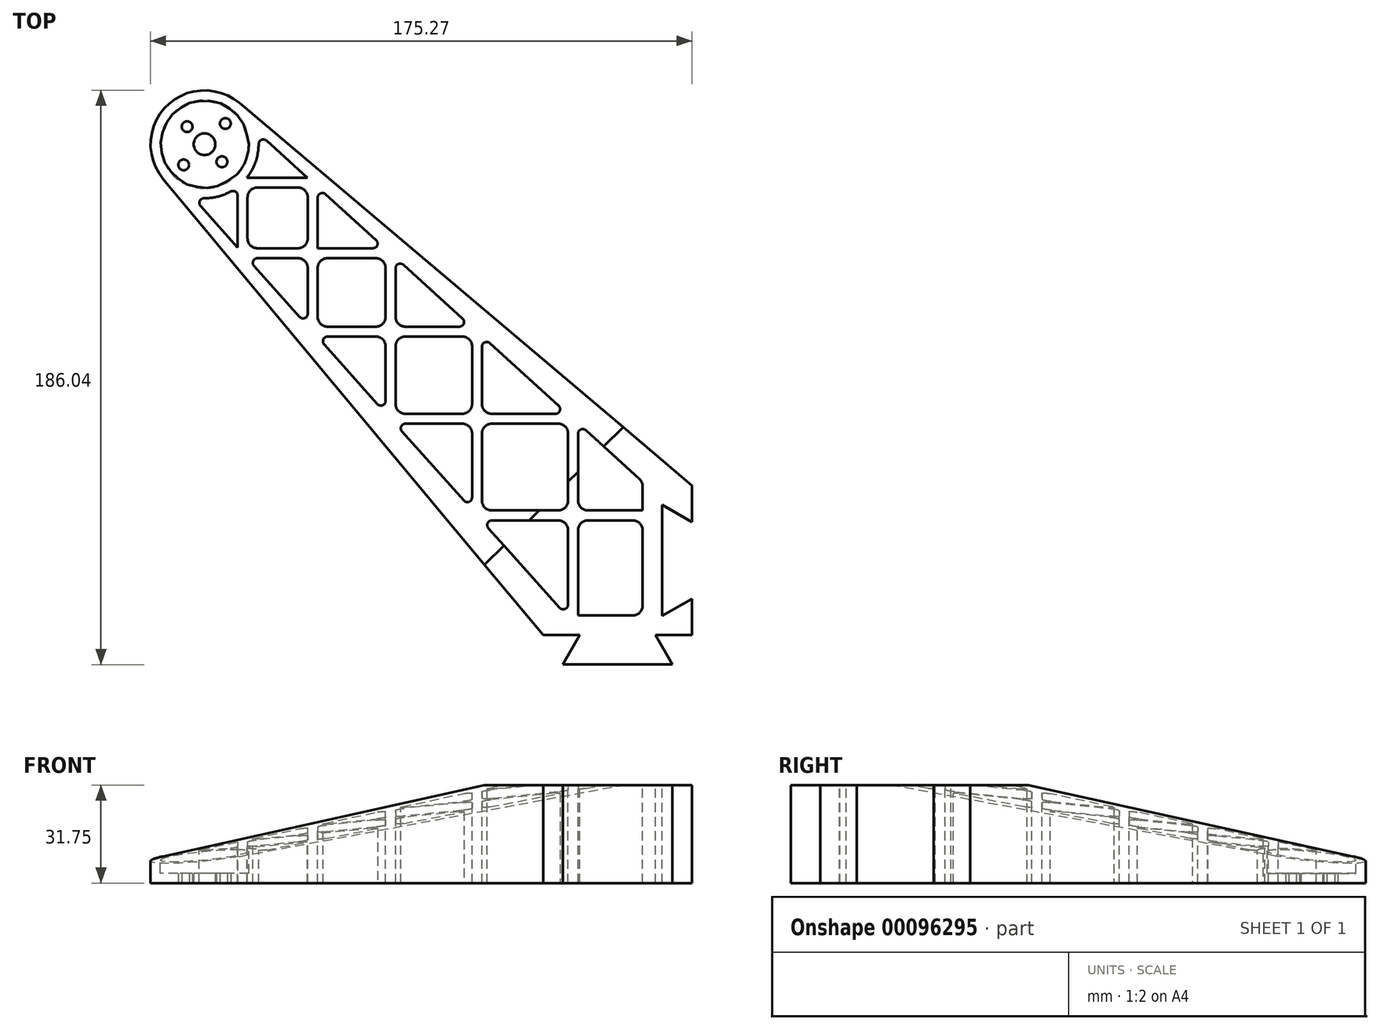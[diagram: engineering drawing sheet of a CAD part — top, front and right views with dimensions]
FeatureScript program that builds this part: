
annotation { "Feature Type Name" : "Feature", "Feature Type Description" : "" }
export const myFeature = defineFeature(function(context is Context, id is Id, definition is map)
    precondition{}
    {
        {
            var Q0;
            Q0=qCreatedBy(makeId("Top.planeOp"),FACE);
            var sketch = newSketch(context, id + "F0", { "sketchPlane" : qUnion([Q0])});
            skCircle(sketch, "E0", {"center": v(-157.77, 159.01) * mm, "radius": 17.5 * mm});
            skLineSegment(sketch, "E1", {"start": v(-157.77, 159.01) * mm, "end": v(0, 0) * mm, "construction": true});
            skLineSegment(sketch, "E2", {"start": v(-171.22, 147.82) * mm, "end": v(-48.17, 0) * mm});
            skLineSegment(sketch, "E3", {"start": v(-146.46, 172.38) * mm, "end": v(0, 48.5) * mm});
            skLineSegment(sketch, "E4", {"start": v(0, 48.5) * mm, "end": v(0, 0) * mm});
            skLineSegment(sketch, "E5", {"start": v(0, 0) * mm, "end": v(-48.17, 0) * mm});
            skSolve(sketch);
        }
        {
            var Q0;
            Q0 = qSketchRegion(id + "F0", true);
            var Q1;
            Q1 = qSketchRegion(id + "F2", true);
            extrude(context, id + "F1", {"entities" : qUnion([Q0, Q1]), "depth" : 31.75 * mm});
        }
        {
            var Q0;
            Q0=makeQuery(id+"F1.opExtrude","CAP_FACE",FACE,{"disambiguationData":[OSD([sQuery(id+"F0.wireOp",EDGE,"E0"),sQuery(id+"F0.wireOp",EDGE,"E2"),sQuery(id+"F0.wireOp",EDGE,"E3"),sQuery(id+"F0.wireOp",EDGE,"E4"),sQuery(id+"F0.wireOp",EDGE,"E5")])],"isStart":false});
            var sketch = newSketch(context, id + "F2", { "sketchPlane" : qUnion([Q0])});
            skCircle(sketch, "E6", {"center": v(-157.77, 159.01) * mm, "radius": 14.33 * mm});
            skSolve(sketch);
        }
        {
            var Q0;
            Q0 = qSketchRegion(id + "F2", true);
            extrude(context, id + "F3", {"entities" : qUnion([Q0]), "operationType" : NewBodyOperationType.REMOVE, "oppositeDirection" : true, "depth" : 28.57 * mm});
        }
        {
            var Q0;
            Q0=makeQuery(id+"F1.opExtrude","CAP_FACE",FACE,{"disambiguationData":[OSD([sQuery(id+"F0.wireOp",EDGE,"E0"),sQuery(id+"F0.wireOp",EDGE,"E2"),sQuery(id+"F0.wireOp",EDGE,"E3"),sQuery(id+"F0.wireOp",EDGE,"E4"),sQuery(id+"F0.wireOp",EDGE,"E5")])],"isStart":false});
            var sketch = newSketch(context, id + "F4", { "sketchPlane" : qUnion([Q0])});
            skLineSegment(sketch, "E7", {"start": v(-36.32, 0) * mm, "end": v(-41.82, -9.52) * mm});
            skLineSegment(sketch, "E8", {"start": v(-41.82, -9.53) * mm, "end": v(-6.35, -9.53) * mm});
            skLineSegment(sketch, "E9", {"start": v(-6.35, -9.53) * mm, "end": v(-11.85, 0) * mm});
            skSolve(sketch);
        }
        {
            var Q0;
            Q0 = qSketchRegion(id + "F4", true);
            var Q1;
            {var subQ0=sQuery(id+"F4.wireOp",EDGE,"E7");Q1=makeQuery(id+"F4.imprint","IMPRINT",FACE,{"disambiguationData":[TD([[makeQuery(id+"F4.imprint","IMPRINT",EDGE,{"derivedFrom":subQ0}),1.0]])]});}
            extrude(context, id + "F5", {"entities" : qUnion([Q0, Q1]), "operationType" : NewBodyOperationType.ADD, "oppositeDirection" : true, "depth" : 31.75 * mm});
        }
        {
            var Q0;
            {var subQ0=sQuery(id+"F0.wireOp",EDGE,"E5");Q0=makeQuery(id+"F5.boolean.opBoolean","MERGE",FACE,{"derivedFrom":[makeQuery(id+"F1.opExtrude","CAP_FACE",FACE,{"disambiguationData":[OSD([sQuery(id+"F0.wireOp",EDGE,"E0"),sQuery(id+"F0.wireOp",EDGE,"E2"),sQuery(id+"F0.wireOp",EDGE,"E3"),sQuery(id+"F0.wireOp",EDGE,"E4"),subQ0])],"isStart":false}),makeQuery(id+"F5.opExtrude","CAP_FACE",FACE,{"disambiguationData":[OSD([subQ0,sQuery(id+"F4.wireOp",EDGE,"E7"),sQuery(id+"F4.wireOp",EDGE,"E8"),sQuery(id+"F4.wireOp",EDGE,"E9")])],"isStart":true})]});}
            var sketch = newSketch(context, id + "F6", { "sketchPlane" : qUnion([Q0])});
            skLineSegment(sketch, "E10", {"start": v(0, 11.8) * mm, "end": v(-9.65, 6.22) * mm});
            skLineSegment(sketch, "E11", {"start": v(-9.65, 6.22) * mm, "end": v(-9.65, 42.27) * mm});
            skLineSegment(sketch, "E12", {"start": v(-9.65, 42.27) * mm, "end": v(0, 36.7) * mm});
            skSolve(sketch);
        }
        {
            var Q0;
            Q0 = qSketchRegion(id + "F6", true);
            var Q1;
            {var subQ0=sQuery(id+"F6.wireOp",EDGE,"E10");Q1=makeQuery(id+"F6.imprint","IMPRINT",FACE,{"disambiguationData":[TD([[makeQuery(id+"F6.imprint","IMPRINT",EDGE,{"derivedFrom":subQ0}),-1.0]])]});}
            extrude(context, id + "F7", {"entities" : qUnion([Q0, Q1]), "operationType" : NewBodyOperationType.REMOVE, "endBound" : BoundingType.THROUGH_ALL, "oppositeDirection" : true, "depth" : 25.4 * mm});
        }
        {
            var Q0;
            {var subQ0=sQuery(id+"F0.wireOp",EDGE,"E5");Q0=makeQuery(id+"F5.boolean.opBoolean","MERGE",FACE,{"derivedFrom":[makeQuery(id+"F1.opExtrude","CAP_FACE",FACE,{"disambiguationData":[OSD([sQuery(id+"F0.wireOp",EDGE,"E0"),sQuery(id+"F0.wireOp",EDGE,"E2"),sQuery(id+"F0.wireOp",EDGE,"E3"),sQuery(id+"F0.wireOp",EDGE,"E4"),subQ0])],"isStart":false}),makeQuery(id+"F5.opExtrude","CAP_FACE",FACE,{"disambiguationData":[OSD([subQ0,sQuery(id+"F4.wireOp",EDGE,"E7"),sQuery(id+"F4.wireOp",EDGE,"E8"),sQuery(id+"F4.wireOp",EDGE,"E9")])],"isStart":true})]});}
            var sketch = newSketch(context, id + "F8", { "sketchPlane" : qUnion([Q0])});
            skCircle(sketch, "E13", {"center": v(-157.77, 159.01) * mm, "radius": 17.5 * mm});
            skLineSegment(sketch, "E14", {"start": v(-40.6, 6.35) * mm, "end": v(-168.45, 149.47) * mm});
            skLineSegment(sketch, "E15", {"start": v(-40.6, 6.35) * mm, "end": v(-16, 6.35) * mm});
            skLineSegment(sketch, "E16", {"start": v(-16, 6.35) * mm, "end": v(-16, 49.7) * mm});
            skLineSegment(sketch, "E17", {"start": v(-16, 49.7) * mm, "end": v(-148.14, 169.62) * mm});
            skSolve(sketch);
        }
        {
            var Q0;
            {var subQ1=sQuery(id+"F8.wireOp",EDGE,"E15");Q0=makeQuery(id+"F8.imprint","IMPRINT",FACE,{"disambiguationData":[TD([[makeQuery(id+"F8.imprint","IMPRINT",EDGE,{"derivedFrom":subQ1}),1.0]])]});}
            extrude(context, id + "F9", {"entities" : qUnion([Q0]), "operationType" : NewBodyOperationType.REMOVE, "endBound" : BoundingType.THROUGH_ALL, "oppositeDirection" : true, "depth" : 28.57 * mm});
        }
        {
            var Q0;
            {var subQ0=sQuery(id+"F0.wireOp",EDGE,"E5");Q0=makeQuery(id+"F5.boolean.opBoolean","MERGE",FACE,{"derivedFrom":[makeQuery(id+"F1.opExtrude","CAP_FACE",FACE,{"disambiguationData":[OSD([sQuery(id+"F0.wireOp",EDGE,"E0"),sQuery(id+"F0.wireOp",EDGE,"E2"),sQuery(id+"F0.wireOp",EDGE,"E3"),sQuery(id+"F0.wireOp",EDGE,"E4"),subQ0])],"isStart":false}),makeQuery(id+"F5.opExtrude","CAP_FACE",FACE,{"disambiguationData":[OSD([subQ0,sQuery(id+"F4.wireOp",EDGE,"E7"),sQuery(id+"F4.wireOp",EDGE,"E8"),sQuery(id+"F4.wireOp",EDGE,"E9")])],"isStart":true})]});}
            var sketch = newSketch(context, id + "F10", { "sketchPlane" : qUnion([Q0])});
            skLineSegment(sketch, "E18", {"start": v(-145.44, 146.6) * mm, "end": v(-122.76, 146.6) * mm, "construction": true});
            skLineSegment(sketch, "E19", {"start": v(-122.76, 146.6) * mm, "end": v(-122.76, 98.33) * mm, "construction": true});
            skLineSegment(sketch, "E20", {"start": v(-122.76, 98.33) * mm, "end": v(-69.58, 98.33) * mm, "construction": true});
            skLineSegment(sketch, "E21", {"start": v(-69.58, 98.33) * mm, "end": v(-69.58, 38.8) * mm, "construction": true});
            skLineSegment(sketch, "E22", {"start": v(-69.58, 38.8) * mm, "end": v(-16, 38.8) * mm, "construction": true});
            skLineSegment(sketch, "E23", {"start": v(-145.44, 146.6) * mm, "end": v(-145.44, 123.71) * mm, "construction": true});
            skLineSegment(sketch, "E24", {"start": v(-145.44, 123.71) * mm, "end": v(-97.56, 123.71) * mm, "construction": true});
            skLineSegment(sketch, "E25", {"start": v(-97.56, 123.71) * mm, "end": v(-97.56, 70.1) * mm, "construction": true});
            skLineSegment(sketch, "E26", {"start": v(-97.56, 70.1) * mm, "end": v(-38.5, 70.1) * mm, "construction": true});
            skLineSegment(sketch, "E27", {"start": v(-38.5, 70.1) * mm, "end": v(-38.5, 6.35) * mm, "construction": true});
            skArc(sketch, "E28.0", {"start": v(-161.75, 141.98) * mm, "mid": v(-145.44, 146.6) * mm, "end": v(-140.7, 162.87) * mm});
            skLineSegment(sketch, "E29.0", {"start": v(-16, 49.7) * mm, "end": v(-140.7, 162.87) * mm});
            skLineSegment(sketch, "E30.0", {"start": v(-40.6, 6.35) * mm, "end": v(-161.75, 141.98) * mm});
            skLineSegment(sketch, "E31.0", {"start": v(-144.01, 148.2) * mm, "end": v(-124.53, 148.2) * mm});
            skLineSegment(sketch, "E32", {"start": v(-147.04, 145.19) * mm, "end": v(-147.04, 125.5) * mm});
            skLineSegment(sketch, "E33.bottom", {"start": v(-121.16, 122.11) * mm, "end": v(-99.16, 122.11) * mm});
            skLineSegment(sketch, "E33.top", {"start": v(-121.16, 99.93) * mm, "end": v(-99.16, 99.93) * mm});
            skLineSegment(sketch, "E33.left", {"start": v(-121.16, 122.11) * mm, "end": v(-121.16, 99.93) * mm});
            skLineSegment(sketch, "E33.right", {"start": v(-99.16, 122.11) * mm, "end": v(-99.16, 99.93) * mm});
            skLineSegment(sketch, "E34.bottom", {"start": v(-143.84, 145) * mm, "end": v(-124.36, 145) * mm});
            skLineSegment(sketch, "E34.top", {"start": v(-143.84, 125.31) * mm, "end": v(-124.36, 125.31) * mm});
            skLineSegment(sketch, "E34.left", {"start": v(-143.84, 145) * mm, "end": v(-143.84, 125.31) * mm});
            skLineSegment(sketch, "E34.right", {"start": v(-124.36, 145) * mm, "end": v(-124.36, 125.31) * mm});
            skLineSegment(sketch, "E35.bottom", {"start": v(-95.96, 96.73) * mm, "end": v(-71.18, 96.73) * mm});
            skLineSegment(sketch, "E35.top", {"start": v(-95.96, 71.7) * mm, "end": v(-71.18, 71.7) * mm});
            skLineSegment(sketch, "E35.left", {"start": v(-95.96, 96.73) * mm, "end": v(-95.96, 71.7) * mm});
            skLineSegment(sketch, "E35.right", {"start": v(-71.18, 96.73) * mm, "end": v(-71.18, 71.7) * mm});
            skLineSegment(sketch, "E36.bottom", {"start": v(-67.98, 68.5) * mm, "end": v(-40.1, 68.5) * mm});
            skLineSegment(sketch, "E36.top", {"start": v(-67.98, 40.4) * mm, "end": v(-40.1, 40.4) * mm});
            skLineSegment(sketch, "E36.left", {"start": v(-67.98, 68.5) * mm, "end": v(-67.98, 40.4) * mm});
            skLineSegment(sketch, "E36.right", {"start": v(-40.1, 68.5) * mm, "end": v(-40.1, 40.4) * mm});
            skLineSegment(sketch, "E37.bottom", {"start": v(-36.89, 37.2) * mm, "end": v(-16, 37.2) * mm});
            skLineSegment(sketch, "E37.left", {"start": v(-36.89, 37.2) * mm, "end": v(-36.89, 6.35) * mm});
            skLineSegment(sketch, "E38.top", {"start": v(-36.89, 40.4) * mm, "end": v(-16, 40.4) * mm});
            skLineSegment(sketch, "E38.left", {"start": v(-36.89, 68.66) * mm, "end": v(-36.89, 40.4) * mm});
            skLineSegment(sketch, "E39.top", {"start": v(-40.1, 37.2) * mm, "end": v(-68.15, 37.2) * mm});
            skLineSegment(sketch, "E39.left", {"start": v(-40.1, 6.35) * mm, "end": v(-40.1, 37.2) * mm});
            skLineSegment(sketch, "E40.top", {"start": v(-71.18, 68.5) * mm, "end": v(-96.13, 68.5) * mm});
            skLineSegment(sketch, "E40.left", {"start": v(-71.18, 40.59) * mm, "end": v(-71.18, 68.5) * mm});
            skLineSegment(sketch, "E41.top", {"start": v(-67.98, 71.7) * mm, "end": v(-40.25, 71.7) * mm});
            skLineSegment(sketch, "E41.left", {"start": v(-67.98, 96.88) * mm, "end": v(-67.98, 71.7) * mm});
            skLineSegment(sketch, "E42.top", {"start": v(-99.16, 96.73) * mm, "end": v(-121.33, 96.73) * mm});
            skLineSegment(sketch, "E42.left", {"start": v(-99.16, 71.9) * mm, "end": v(-99.16, 96.73) * mm});
            skLineSegment(sketch, "E43.top", {"start": v(-95.96, 99.93) * mm, "end": v(-71.35, 99.93) * mm});
            skLineSegment(sketch, "E43.left", {"start": v(-95.96, 122.26) * mm, "end": v(-95.96, 99.93) * mm});
            skLineSegment(sketch, "E44.top", {"start": v(-121.16, 125.31) * mm, "end": v(-99.32, 125.31) * mm});
            skLineSegment(sketch, "E44.left", {"start": v(-121.16, 145.14) * mm, "end": v(-121.16, 125.31) * mm});
            skLineSegment(sketch, "E45.top", {"start": v(-124.36, 122.11) * mm, "end": v(-144.01, 122.11) * mm});
            skLineSegment(sketch, "E45.left", {"start": v(-124.36, 100.12) * mm, "end": v(-124.36, 122.11) * mm});
            skLineSegment(sketch, "E46.0", {"start": v(-16, 6.35) * mm, "end": v(-16, 49.7) * mm});
            skLineSegment(sketch, "E47.0", {"start": v(-40.6, 6.35) * mm, "end": v(-16, 6.35) * mm});
            skSolve(sketch);
        }
        {
            var Q0;
            {var subQ1=sQuery(id+"F10.wireOp",EDGE,"E31.0");Q0=makeQuery(id+"F10.imprint","IMPRINT",FACE,{"disambiguationData":[TD([[makeQuery(id+"F10.imprint","IMPRINT",EDGE,{"derivedFrom":subQ1}),-1.0]])]});}
            var Q1;
            {var subQ0=sQuery(id+"F0.wireOp",EDGE,"E5");Q1=makeQuery(id+"F5.boolean.opBoolean","MERGE",FACE,{"derivedFrom":[makeQuery(id+"F1.opExtrude","CAP_FACE",FACE,{"disambiguationData":[OSD([sQuery(id+"F0.wireOp",EDGE,"E0"),sQuery(id+"F0.wireOp",EDGE,"E2"),sQuery(id+"F0.wireOp",EDGE,"E3"),sQuery(id+"F0.wireOp",EDGE,"E4"),subQ0])],"isStart":true}),makeQuery(id+"F5.opExtrude","CAP_FACE",FACE,{"disambiguationData":[OSD([subQ0,sQuery(id+"F4.wireOp",EDGE,"E7"),sQuery(id+"F4.wireOp",EDGE,"E8"),sQuery(id+"F4.wireOp",EDGE,"E9")])],"isStart":false})]});}
            extrude(context, id + "F11", {"entities" : qUnion([Q0]), "operationType" : NewBodyOperationType.ADD, "endBound" : BoundingType.UP_TO_SURFACE, "oppositeDirection" : true, "endBoundEntityFace" : qUnion([Q1]), "depth" : 25.4 * mm});
        }
        {
            var Q0;
            Q0=makeQuery(id+"F11.opExtrude","SWEPT_EDGE",EDGE,{"disambiguationData":[OSD([sQuery(id+"F10.wireOp",EDGE,"E28.0"),sQuery(id+"F10.wireOp",EDGE,"E32")])]});
            var Q1;
            Q1=makeQuery(id+"F9.boolean.opBoolean","COPY",EDGE,{"derivedFrom":makeQuery(id+"F9.opExtrude","SWEPT_EDGE",EDGE,{"disambiguationData":[OSD([sQuery(id+"F8.wireOp",EDGE,"E13"),sQuery(id+"F8.wireOp",EDGE,"E14")])]})});
            var Q2;
            Q2=makeQuery(id+"F11.opExtrude","SWEPT_EDGE",EDGE,{"disambiguationData":[OSD([sQuery(id+"F10.wireOp",EDGE,"E30.0"),sQuery(id+"F10.wireOp",EDGE,"E32")])]});
            var Q3;
            Q3=makeQuery(id+"F9.boolean.opBoolean","COPY",EDGE,{"derivedFrom":makeQuery(id+"F9.opExtrude","SWEPT_EDGE",EDGE,{"disambiguationData":[OSD([sQuery(id+"F8.wireOp",EDGE,"E13"),sQuery(id+"F8.wireOp",EDGE,"E17")])]})});
            var Q4;
            Q4=makeQuery(id+"F11.opExtrude","SWEPT_EDGE",EDGE,{"disambiguationData":[OSD([sQuery(id+"F10.wireOp",EDGE,"E28.0"),sQuery(id+"F10.wireOp",EDGE,"E31.0")])]});
            var Q5;
            Q5=makeQuery(id+"F11.opExtrude","SWEPT_EDGE",EDGE,{"disambiguationData":[OSD([sQuery(id+"F10.wireOp",EDGE,"E29.0"),sQuery(id+"F10.wireOp",EDGE,"E31.0")])]});
            fillet(context, id + "F12", {"entities" : qUnion([Q0, Q1, Q2, Q3, Q4, Q5]), "radius" : 1.52 * mm, "tangentPropagation" : true, "allowEdgeOverflow" : false});
        }
        {
            var Q0;
            Q0=makeQuery(id+"F11.opExtrude","SWEPT_EDGE",EDGE,{"disambiguationData":[OSD([sQuery(id+"F10.wireOp",EDGE,"E30.0"),sQuery(id+"F10.wireOp",EDGE,"E45.left")])]});
            var Q1;
            Q1=makeQuery(id+"F11.opExtrude","SWEPT_EDGE",EDGE,{"disambiguationData":[OSD([sQuery(id+"F10.wireOp",EDGE,"E30.0"),sQuery(id+"F10.wireOp",EDGE,"E45.top")])]});
            var Q2;
            Q2=makeQuery(id+"F11.opExtrude","SWEPT_EDGE",EDGE,{"disambiguationData":[OSD([sQuery(id+"F10.wireOp",EDGE,"E30.0"),sQuery(id+"F10.wireOp",EDGE,"E42.top")])]});
            var Q3;
            Q3=makeQuery(id+"F11.opExtrude","SWEPT_EDGE",EDGE,{"disambiguationData":[OSD([sQuery(id+"F10.wireOp",EDGE,"E30.0"),sQuery(id+"F10.wireOp",EDGE,"E42.left")])]});
            var Q4;
            Q4=makeQuery(id+"F11.opExtrude","SWEPT_EDGE",EDGE,{"disambiguationData":[OSD([sQuery(id+"F10.wireOp",EDGE,"E30.0"),sQuery(id+"F10.wireOp",EDGE,"E40.left")])]});
            var Q5;
            Q5=makeQuery(id+"F11.opExtrude","SWEPT_EDGE",EDGE,{"disambiguationData":[OSD([sQuery(id+"F10.wireOp",EDGE,"E30.0"),sQuery(id+"F10.wireOp",EDGE,"E40.top")])]});
            var Q6;
            Q6=makeQuery(id+"F11.opExtrude","SWEPT_EDGE",EDGE,{"disambiguationData":[OSD([sQuery(id+"F10.wireOp",EDGE,"E29.0"),sQuery(id+"F10.wireOp",EDGE,"E43.left")])]});
            var Q7;
            Q7=makeQuery(id+"F11.opExtrude","SWEPT_EDGE",EDGE,{"disambiguationData":[OSD([sQuery(id+"F10.wireOp",EDGE,"E29.0"),sQuery(id+"F10.wireOp",EDGE,"E44.left")])]});
            var Q8;
            Q8=makeQuery(id+"F11.opExtrude","SWEPT_EDGE",EDGE,{"disambiguationData":[OSD([sQuery(id+"F10.wireOp",EDGE,"E29.0"),sQuery(id+"F10.wireOp",EDGE,"E41.left")])]});
            var Q9;
            Q9=makeQuery(id+"F11.opExtrude","SWEPT_EDGE",EDGE,{"disambiguationData":[OSD([sQuery(id+"F10.wireOp",EDGE,"E29.0"),sQuery(id+"F10.wireOp",EDGE,"E44.top")])]});
            var Q10;
            Q10=makeQuery(id+"F11.opExtrude","SWEPT_EDGE",EDGE,{"disambiguationData":[OSD([sQuery(id+"F10.wireOp",EDGE,"E29.0"),sQuery(id+"F10.wireOp",EDGE,"E43.top")])]});
            var Q11;
            Q11=makeQuery(id+"F11.opExtrude","SWEPT_EDGE",EDGE,{"disambiguationData":[OSD([sQuery(id+"F10.wireOp",EDGE,"E29.0"),sQuery(id+"F10.wireOp",EDGE,"E41.top")])]});
            var Q12;
            Q12=makeQuery(id+"F11.opExtrude","SWEPT_EDGE",EDGE,{"disambiguationData":[OSD([sQuery(id+"F10.wireOp",EDGE,"E30.0"),sQuery(id+"F10.wireOp",EDGE,"E39.top")])]});
            var Q13;
            Q13=makeQuery(id+"F11.opExtrude","SWEPT_EDGE",EDGE,{"disambiguationData":[OSD([sQuery(id+"F10.wireOp",EDGE,"E29.0"),sQuery(id+"F10.wireOp",EDGE,"E38.left")])]});
            fillet(context, id + "F13", {"entities" : qUnion([Q0, Q1, Q2, Q3, Q4, Q5, Q6, Q7, Q8, Q9, Q10, Q11, Q12, Q13]), "radius" : 1.52 * mm, "tangentPropagation" : true, "allowEdgeOverflow" : false});
        }
        {
            var Q0;
            Q0=makeQuery(id+"F11.opExtrude","SWEPT_EDGE",EDGE,{"disambiguationData":[OSD([sQuery(id+"F10.wireOp",EDGE,"E36.top"),sQuery(id+"F10.wireOp",EDGE,"E36.right")])]});
            var Q1;
            Q1=makeQuery(id+"F11.opExtrude","SWEPT_EDGE",EDGE,{"disambiguationData":[OSD([sQuery(id+"F10.wireOp",EDGE,"E36.top"),sQuery(id+"F10.wireOp",EDGE,"E36.left")])]});
            var Q2;
            Q2=makeQuery(id+"F11.opExtrude","SWEPT_EDGE",EDGE,{"disambiguationData":[OSD([sQuery(id+"F10.wireOp",EDGE,"E36.bottom"),sQuery(id+"F10.wireOp",EDGE,"E36.left")])]});
            var Q3;
            Q3=makeQuery(id+"F11.opExtrude","SWEPT_EDGE",EDGE,{"disambiguationData":[OSD([sQuery(id+"F10.wireOp",EDGE,"E36.bottom"),sQuery(id+"F10.wireOp",EDGE,"E36.right")])]});
            var Q4;
            Q4=makeQuery(id+"F11.opExtrude","SWEPT_EDGE",EDGE,{"disambiguationData":[OSD([sQuery(id+"F10.wireOp",EDGE,"E39.top"),sQuery(id+"F10.wireOp",EDGE,"E39.left")])]});
            var Q5;
            Q5=makeQuery(id+"F11.opExtrude","SWEPT_EDGE",EDGE,{"disambiguationData":[OSD([sQuery(id+"F10.wireOp",EDGE,"E37.bottom"),sQuery(id+"F10.wireOp",EDGE,"E46.0")])]});
            var Q6;
            Q6=makeQuery(id+"F11.opExtrude","SWEPT_EDGE",EDGE,{"disambiguationData":[OSD([sQuery(id+"F10.wireOp",EDGE,"E37.bottom"),sQuery(id+"F10.wireOp",EDGE,"E37.left")])]});
            var Q7;
            Q7=makeQuery(id+"F11.opExtrude","SWEPT_EDGE",EDGE,{"disambiguationData":[OSD([sQuery(id+"F10.wireOp",EDGE,"E37.left"),sQuery(id+"F10.wireOp",EDGE,"E47.0")])]});
            var Q8;
            Q8=makeQuery(id+"F9.boolean.opBoolean","COPY",EDGE,{"derivedFrom":makeQuery(id+"F9.opExtrude","SWEPT_EDGE",EDGE,{"disambiguationData":[OSD([sQuery(id+"F8.wireOp",EDGE,"E15"),sQuery(id+"F8.wireOp",EDGE,"E16")])]})});
            var Q9;
            Q9=makeQuery(id+"F11.opExtrude","SWEPT_EDGE",EDGE,{"disambiguationData":[OSD([sQuery(id+"F10.wireOp",EDGE,"E40.top"),sQuery(id+"F10.wireOp",EDGE,"E40.left")])]});
            var Q10;
            Q10=makeQuery(id+"F11.opExtrude","SWEPT_EDGE",EDGE,{"disambiguationData":[OSD([sQuery(id+"F10.wireOp",EDGE,"E35.top"),sQuery(id+"F10.wireOp",EDGE,"E35.right")])]});
            var Q11;
            Q11=makeQuery(id+"F11.opExtrude","SWEPT_EDGE",EDGE,{"disambiguationData":[OSD([sQuery(id+"F10.wireOp",EDGE,"E41.top"),sQuery(id+"F10.wireOp",EDGE,"E41.left")])]});
            var Q12;
            Q12=makeQuery(id+"F11.opExtrude","SWEPT_EDGE",EDGE,{"disambiguationData":[OSD([sQuery(id+"F10.wireOp",EDGE,"E35.top"),sQuery(id+"F10.wireOp",EDGE,"E35.left")])]});
            var Q13;
            Q13=makeQuery(id+"F11.opExtrude","SWEPT_EDGE",EDGE,{"disambiguationData":[OSD([sQuery(id+"F10.wireOp",EDGE,"E35.bottom"),sQuery(id+"F10.wireOp",EDGE,"E35.left")])]});
            var Q14;
            Q14=makeQuery(id+"F11.opExtrude","SWEPT_EDGE",EDGE,{"disambiguationData":[OSD([sQuery(id+"F10.wireOp",EDGE,"E35.bottom"),sQuery(id+"F10.wireOp",EDGE,"E35.right")])]});
            var Q15;
            Q15=makeQuery(id+"F11.opExtrude","SWEPT_EDGE",EDGE,{"disambiguationData":[OSD([sQuery(id+"F10.wireOp",EDGE,"E42.top"),sQuery(id+"F10.wireOp",EDGE,"E42.left")])]});
            var Q16;
            Q16=makeQuery(id+"F11.opExtrude","SWEPT_EDGE",EDGE,{"disambiguationData":[OSD([sQuery(id+"F10.wireOp",EDGE,"E33.bottom"),sQuery(id+"F10.wireOp",EDGE,"E33.right")])]});
            var Q17;
            Q17=makeQuery(id+"F11.opExtrude","SWEPT_EDGE",EDGE,{"disambiguationData":[OSD([sQuery(id+"F10.wireOp",EDGE,"E45.top"),sQuery(id+"F10.wireOp",EDGE,"E45.left")])]});
            var Q18;
            Q18=makeQuery(id+"F11.opExtrude","SWEPT_EDGE",EDGE,{"disambiguationData":[OSD([sQuery(id+"F10.wireOp",EDGE,"E34.bottom"),sQuery(id+"F10.wireOp",EDGE,"E34.right")])]});
            var Q19;
            Q19=makeQuery(id+"F11.opExtrude","SWEPT_EDGE",EDGE,{"disambiguationData":[OSD([sQuery(id+"F10.wireOp",EDGE,"E43.top"),sQuery(id+"F10.wireOp",EDGE,"E43.left")])]});
            var Q20;
            Q20=makeQuery(id+"F11.opExtrude","SWEPT_EDGE",EDGE,{"disambiguationData":[OSD([sQuery(id+"F10.wireOp",EDGE,"E33.top"),sQuery(id+"F10.wireOp",EDGE,"E33.left")])]});
            var Q21;
            Q21=makeQuery(id+"F11.opExtrude","SWEPT_EDGE",EDGE,{"disambiguationData":[OSD([sQuery(id+"F10.wireOp",EDGE,"E34.top"),sQuery(id+"F10.wireOp",EDGE,"E34.left")])]});
            var Q22;
            Q22=makeQuery(id+"F11.opExtrude","SWEPT_EDGE",EDGE,{"disambiguationData":[OSD([sQuery(id+"F10.wireOp",EDGE,"E33.top"),sQuery(id+"F10.wireOp",EDGE,"E33.right")])]});
            var Q23;
            Q23=makeQuery(id+"F11.opExtrude","SWEPT_EDGE",EDGE,{"disambiguationData":[OSD([sQuery(id+"F10.wireOp",EDGE,"E34.top"),sQuery(id+"F10.wireOp",EDGE,"E34.right")])]});
            var Q24;
            Q24=makeQuery(id+"F11.opExtrude","SWEPT_EDGE",EDGE,{"disambiguationData":[OSD([sQuery(id+"F10.wireOp",EDGE,"E33.bottom"),sQuery(id+"F10.wireOp",EDGE,"E33.left")])]});
            var Q25;
            Q25=makeQuery(id+"F11.opExtrude","SWEPT_EDGE",EDGE,{"disambiguationData":[OSD([sQuery(id+"F10.wireOp",EDGE,"E34.bottom"),sQuery(id+"F10.wireOp",EDGE,"E34.left")])]});
            var Q26;
            Q26=makeQuery(id+"F11.opExtrude","SWEPT_EDGE",EDGE,{"disambiguationData":[OSD([sQuery(id+"F10.wireOp",EDGE,"E38.top"),sQuery(id+"F10.wireOp",EDGE,"E38.left")])]});
            var Q27;
            Q27=makeQuery(id+"F9.boolean.opBoolean","COPY",EDGE,{"derivedFrom":makeQuery(id+"F9.opExtrude","SWEPT_EDGE",EDGE,{"disambiguationData":[OSD([sQuery(id+"F8.wireOp",EDGE,"E16"),sQuery(id+"F8.wireOp",EDGE,"E17")])]})});
            var Q28;
            Q28=makeQuery(id+"F11.opExtrude","SWEPT_EDGE",EDGE,{"disambiguationData":[OSD([sQuery(id+"F10.wireOp",EDGE,"E38.top"),sQuery(id+"F10.wireOp",EDGE,"E46.0")])]});
            fillet(context, id + "F14", {"entities" : qUnion([Q0, Q1, Q2, Q3, Q4, Q5, Q6, Q7, Q8, Q9, Q10, Q11, Q12, Q13, Q14, Q15, Q16, Q17, Q18, Q19, Q20, Q21, Q22, Q23, Q24, Q25, Q26, Q27, Q28]), "radius" : 3.17 * mm, "tangentPropagation" : true, "allowEdgeOverflow" : false});
        }
        {
            var Q0;
            {var subQ0=sQuery(id+"F0.wireOp",EDGE,"E5");Q0=makeQuery(id+"F11.boolean.opBoolean","MERGE",FACE,{"derivedFrom":[makeQuery(id+"F5.boolean.opBoolean","MERGE",FACE,{"derivedFrom":[makeQuery(id+"F1.opExtrude","CAP_FACE",FACE,{"disambiguationData":[OSD([sQuery(id+"F0.wireOp",EDGE,"E0"),sQuery(id+"F0.wireOp",EDGE,"E2"),sQuery(id+"F0.wireOp",EDGE,"E3"),sQuery(id+"F0.wireOp",EDGE,"E4"),subQ0])],"isStart":false}),makeQuery(id+"F5.opExtrude","CAP_FACE",FACE,{"disambiguationData":[OSD([subQ0,sQuery(id+"F4.wireOp",EDGE,"E7"),sQuery(id+"F4.wireOp",EDGE,"E8"),sQuery(id+"F4.wireOp",EDGE,"E9")])],"isStart":true})]}),makeQuery(id+"F11.opExtrude","CAP_FACE",FACE,{"disambiguationData":[OSD([sQuery(id+"F10.wireOp",EDGE,"E28.0"),sQuery(id+"F10.wireOp",EDGE,"E29.0"),sQuery(id+"F10.wireOp",EDGE,"E30.0"),sQuery(id+"F10.wireOp",EDGE,"E31.0"),sQuery(id+"F10.wireOp",EDGE,"E32"),sQuery(id+"F10.wireOp",EDGE,"E33.bottom"),sQuery(id+"F10.wireOp",EDGE,"E33.top"),sQuery(id+"F10.wireOp",EDGE,"E33.left"),sQuery(id+"F10.wireOp",EDGE,"E33.right"),sQuery(id+"F10.wireOp",EDGE,"E34.bottom"),sQuery(id+"F10.wireOp",EDGE,"E34.top"),sQuery(id+"F10.wireOp",EDGE,"E34.left"),sQuery(id+"F10.wireOp",EDGE,"E34.right"),sQuery(id+"F10.wireOp",EDGE,"E35.bottom"),sQuery(id+"F10.wireOp",EDGE,"E35.top"),sQuery(id+"F10.wireOp",EDGE,"E35.left"),sQuery(id+"F10.wireOp",EDGE,"E35.right"),sQuery(id+"F10.wireOp",EDGE,"E36.bottom"),sQuery(id+"F10.wireOp",EDGE,"E36.top"),sQuery(id+"F10.wireOp",EDGE,"E36.left"),sQuery(id+"F10.wireOp",EDGE,"E36.right"),sQuery(id+"F10.wireOp",EDGE,"E37.bottom"),sQuery(id+"F10.wireOp",EDGE,"E37.left"),sQuery(id+"F10.wireOp",EDGE,"E38.top"),sQuery(id+"F10.wireOp",EDGE,"E38.left"),sQuery(id+"F10.wireOp",EDGE,"E39.top"),sQuery(id+"F10.wireOp",EDGE,"E39.left"),sQuery(id+"F10.wireOp",EDGE,"E40.top"),sQuery(id+"F10.wireOp",EDGE,"E40.left"),sQuery(id+"F10.wireOp",EDGE,"E41.top"),sQuery(id+"F10.wireOp",EDGE,"E41.left"),sQuery(id+"F10.wireOp",EDGE,"E42.top"),sQuery(id+"F10.wireOp",EDGE,"E42.left"),sQuery(id+"F10.wireOp",EDGE,"E43.top"),sQuery(id+"F10.wireOp",EDGE,"E43.left"),sQuery(id+"F10.wireOp",EDGE,"E44.top"),sQuery(id+"F10.wireOp",EDGE,"E44.left"),sQuery(id+"F10.wireOp",EDGE,"E45.top"),sQuery(id+"F10.wireOp",EDGE,"E45.left"),sQuery(id+"F10.wireOp",EDGE,"E46.0"),sQuery(id+"F10.wireOp",EDGE,"E47.0")])],"isStart":true})]});}
            var sketch = newSketch(context, id + "F15", { "sketchPlane" : qUnion([Q0])});
            skArc(sketch, "E48", {"start": v(-42.88, 8.9) * mm, "mid": v(-41.12, 8.48) * mm, "end": v(-40.1, 9.97) * mm});
            skLineSegment(sketch, "E49.0", {"start": v(-40.1, 6.35) * mm, "end": v(-40.1, 34.02) * mm});
            skLineSegment(sketch, "E49.1", {"start": v(-40.6, 6.35) * mm, "end": v(-65.88, 34.66) * mm});
            skLineSegment(sketch, "E49.2", {"start": v(-40.6, 6.35) * mm, "end": v(-40.1, 6.35) * mm});
            skSolve(sketch);
        }
        {
            var Q0;
            Q0 = qSketchRegion(id + "F15", true);
            var Q1;
            {var subQ0=sQuery(id+"F4.wireOp",EDGE,"E9");var subQ1=sQuery(id+"F4.wireOp",EDGE,"E8");var subQ2=sQuery(id+"F4.wireOp",EDGE,"E7");var subQ3=sQuery(id+"F0.wireOp",EDGE,"E5");var subQ4=sQuery(id+"F0.wireOp",EDGE,"E4");var subQ5=sQuery(id+"F0.wireOp",EDGE,"E3");var subQ6=sQuery(id+"F0.wireOp",EDGE,"E2");var subQ7=sQuery(id+"F0.wireOp",EDGE,"E0");Q1=makeQuery(id+"F11.boolean.opBoolean","MERGE",FACE,{"derivedFrom":[makeQuery(id+"F5.boolean.opBoolean","MERGE",FACE,{"derivedFrom":[makeQuery(id+"F1.opExtrude","CAP_FACE",FACE,{"disambiguationData":[OSD([subQ7,subQ6,subQ5,subQ4,subQ3])],"isStart":true}),makeQuery(id+"F5.opExtrude","CAP_FACE",FACE,{"disambiguationData":[OSD([subQ3,subQ2,subQ1,subQ0])],"isStart":false})]}),makeQuery(id+"F11.opExtrude","CAP_FACE",FACE,{"disambiguationData":[OSD([subQ7,subQ6,subQ5,subQ4,subQ3,subQ2,subQ1,subQ0])],"isStart":false})]});}
            extrude(context, id + "F16", {"entities" : qUnion([Q0]), "operationType" : NewBodyOperationType.ADD, "endBound" : BoundingType.UP_TO_SURFACE, "oppositeDirection" : true, "endBoundEntityFace" : qUnion([Q1]), "depth" : 25.4 * mm});
        }
        {
            var Q0;
            {var subQ0=sQuery(id+"F0.wireOp",EDGE,"E5");Q0=makeQuery(id+"F16.boolean.opBoolean","MERGE",FACE,{"derivedFrom":[makeQuery(id+"F11.boolean.opBoolean","MERGE",FACE,{"derivedFrom":[makeQuery(id+"F5.boolean.opBoolean","MERGE",FACE,{"derivedFrom":[makeQuery(id+"F1.opExtrude","CAP_FACE",FACE,{"disambiguationData":[OSD([sQuery(id+"F0.wireOp",EDGE,"E0"),sQuery(id+"F0.wireOp",EDGE,"E2"),sQuery(id+"F0.wireOp",EDGE,"E3"),sQuery(id+"F0.wireOp",EDGE,"E4"),subQ0])],"isStart":false}),makeQuery(id+"F5.opExtrude","CAP_FACE",FACE,{"disambiguationData":[OSD([subQ0,sQuery(id+"F4.wireOp",EDGE,"E7"),sQuery(id+"F4.wireOp",EDGE,"E8"),sQuery(id+"F4.wireOp",EDGE,"E9")])],"isStart":true})]}),makeQuery(id+"F11.opExtrude","CAP_FACE",FACE,{"disambiguationData":[OSD([sQuery(id+"F10.wireOp",EDGE,"E28.0"),sQuery(id+"F10.wireOp",EDGE,"E29.0"),sQuery(id+"F10.wireOp",EDGE,"E30.0"),sQuery(id+"F10.wireOp",EDGE,"E31.0"),sQuery(id+"F10.wireOp",EDGE,"E32"),sQuery(id+"F10.wireOp",EDGE,"E33.bottom"),sQuery(id+"F10.wireOp",EDGE,"E33.top"),sQuery(id+"F10.wireOp",EDGE,"E33.left"),sQuery(id+"F10.wireOp",EDGE,"E33.right"),sQuery(id+"F10.wireOp",EDGE,"E34.bottom"),sQuery(id+"F10.wireOp",EDGE,"E34.top"),sQuery(id+"F10.wireOp",EDGE,"E34.left"),sQuery(id+"F10.wireOp",EDGE,"E34.right"),sQuery(id+"F10.wireOp",EDGE,"E35.bottom"),sQuery(id+"F10.wireOp",EDGE,"E35.top"),sQuery(id+"F10.wireOp",EDGE,"E35.left"),sQuery(id+"F10.wireOp",EDGE,"E35.right"),sQuery(id+"F10.wireOp",EDGE,"E36.bottom"),sQuery(id+"F10.wireOp",EDGE,"E36.top"),sQuery(id+"F10.wireOp",EDGE,"E36.left"),sQuery(id+"F10.wireOp",EDGE,"E36.right"),sQuery(id+"F10.wireOp",EDGE,"E37.bottom"),sQuery(id+"F10.wireOp",EDGE,"E37.left"),sQuery(id+"F10.wireOp",EDGE,"E38.top"),sQuery(id+"F10.wireOp",EDGE,"E38.left"),sQuery(id+"F10.wireOp",EDGE,"E39.top"),sQuery(id+"F10.wireOp",EDGE,"E39.left"),sQuery(id+"F10.wireOp",EDGE,"E40.top"),sQuery(id+"F10.wireOp",EDGE,"E40.left"),sQuery(id+"F10.wireOp",EDGE,"E41.top"),sQuery(id+"F10.wireOp",EDGE,"E41.left"),sQuery(id+"F10.wireOp",EDGE,"E42.top"),sQuery(id+"F10.wireOp",EDGE,"E42.left"),sQuery(id+"F10.wireOp",EDGE,"E43.top"),sQuery(id+"F10.wireOp",EDGE,"E43.left"),sQuery(id+"F10.wireOp",EDGE,"E44.top"),sQuery(id+"F10.wireOp",EDGE,"E44.left"),sQuery(id+"F10.wireOp",EDGE,"E45.top"),sQuery(id+"F10.wireOp",EDGE,"E45.left"),sQuery(id+"F10.wireOp",EDGE,"E46.0"),sQuery(id+"F10.wireOp",EDGE,"E47.0")])],"isStart":true})]}),makeQuery(id+"F16.opExtrude","CAP_FACE",FACE,{"disambiguationData":[OSD([sQuery(id+"F15.wireOp",EDGE,"E48"),sQuery(id+"F15.wireOp",EDGE,"E49.0"),sQuery(id+"F15.wireOp",EDGE,"E49.1"),sQuery(id+"F15.wireOp",EDGE,"E49.2")])],"isStart":true})]});}
            var sketch = newSketch(context, id + "F17", { "sketchPlane" : qUnion([Q0])});
            skLineSegment(sketch, "E50", {"start": v(-157.77, 159.01) * mm, "end": v(0, 0) * mm, "construction": true});
            skSolve(sketch);
        }
        {
            var Q0;
            Q0=sQuery(id+"F17.wireOp",EDGE,"E50");
            var Q1;
            Q1=makeQuery(id+"F1.opExtrude","SWEPT_EDGE",EDGE,{"disambiguationData":[OSD([sQuery(id+"F0.wireOp",EDGE,"E4"),sQuery(id+"F0.wireOp",EDGE,"E5")])]});
            cPlane(context, id + "F18", {"entities" : qUnion([Q0, Q1]), "cplaneType" : CPlaneType.LINE_ANGLE, "offset" : 152.4 * mm, "angle" : 0 * degree, "width" : 152.4 * mm, "height" : 152.4 * mm});
        }
        {
            var Q0;
            Q0=qCreatedBy(id+"F18.planeOp",FACE);
            var sketch = newSketch(context, id + "F19", { "sketchPlane" : qUnion([Q0])});
            skLineSegment(sketch, "E51.0.0", {"start": v(225.53, 0) * mm, "end": v(241.5, 0) * mm});
            skLineSegment(sketch, "E51.0.2", {"start": v(241.5, 31.75) * mm, "end": v(225.53, 31.75) * mm});
            skLineSegment(sketch, "E52.0", {"start": v(224, 31.75) * mm, "end": v(0, 31.75) * mm, "construction": true});
            skLineSegment(sketch, "E53", {"start": v(241.5, 6.35) * mm, "end": v(63.5, 31.75) * mm});
            skLineSegment(sketch, "E54", {"start": v(63.5, 31.75) * mm, "end": v(241.5, 31.75) * mm});
            skLineSegment(sketch, "E55", {"start": v(241.5, 6.35) * mm, "end": v(241.5, 31.75) * mm});
            skSolve(sketch);
        }
        {
            var Q0;
            Q0 = qSketchRegion(id + "F19", true);
            extrude(context, id + "F20", {"entities" : qUnion([Q0]), "operationType" : NewBodyOperationType.REMOVE, "endBound" : BoundingType.THROUGH_ALL, "oppositeDirection" : true, "depth" : 25.4 * mm, "hasSecondDirection" : true, "secondDirectionBound" : SecondDirectionBoundingType.THROUGH_ALL, "secondDirectionOppositeDirection" : false, "secondDirectionDepth" : 25.4 * mm});
        }
        {
            var Q0;
            {var subQ0=sQuery(id+"F4.wireOp",EDGE,"E9");var subQ1=sQuery(id+"F4.wireOp",EDGE,"E8");var subQ2=sQuery(id+"F4.wireOp",EDGE,"E7");var subQ3=sQuery(id+"F0.wireOp",EDGE,"E5");var subQ4=sQuery(id+"F0.wireOp",EDGE,"E4");var subQ5=sQuery(id+"F0.wireOp",EDGE,"E3");var subQ6=sQuery(id+"F0.wireOp",EDGE,"E2");var subQ7=sQuery(id+"F0.wireOp",EDGE,"E0");Q0=makeQuery(id+"F16.boolean.opBoolean","MERGE",FACE,{"derivedFrom":[makeQuery(id+"F11.boolean.opBoolean","MERGE",FACE,{"derivedFrom":[makeQuery(id+"F5.boolean.opBoolean","MERGE",FACE,{"derivedFrom":[makeQuery(id+"F1.opExtrude","CAP_FACE",FACE,{"disambiguationData":[OSD([subQ7,subQ6,subQ5,subQ4,subQ3])],"isStart":true}),makeQuery(id+"F5.opExtrude","CAP_FACE",FACE,{"disambiguationData":[OSD([subQ3,subQ2,subQ1,subQ0])],"isStart":false})]}),makeQuery(id+"F11.opExtrude","CAP_FACE",FACE,{"disambiguationData":[OSD([subQ7,subQ6,subQ5,subQ4,subQ3,subQ2,subQ1,subQ0])],"isStart":false})]}),makeQuery(id+"F16.opExtrude","CAP_FACE",FACE,{"disambiguationData":[OSD([subQ7,subQ6,subQ5,subQ4,subQ3,subQ2,subQ1,subQ0])],"isStart":false})]});}
            var sketch = newSketch(context, id + "F21", { "sketchPlane" : qUnion([Q0])});
            skCircle(sketch, "E56", {"center": v(-157.77, -159.01) * mm, "radius": 3.5 * mm});
            skCircle(sketch, "E57", {"center": v(-152.13, -153.34) * mm, "radius": 1.75 * mm});
            skCircle(sketch, "E58", {"center": v(-163.4, -164.7) * mm, "radius": 1.75 * mm});
            skCircle(sketch, "E59", {"center": v(-151.02, -165.7) * mm, "radius": 1.75 * mm});
            skCircle(sketch, "E60", {"center": v(-164.51, -152.32) * mm, "radius": 1.75 * mm});
            skLineSegment(sketch, "E61", {"start": v(-164.51, -152.32) * mm, "end": v(-151.02, -165.7) * mm, "construction": true});
            skLineSegment(sketch, "E62", {"start": v(-163.4, -164.7) * mm, "end": v(-152.13, -153.34) * mm, "construction": true});
            skSolve(sketch);
        }
        {
            var Q0;
            Q0 = qSketchRegion(id + "F21", true);
            extrude(context, id + "F22", {"entities" : qUnion([Q0]), "operationType" : NewBodyOperationType.REMOVE, "endBound" : BoundingType.THROUGH_ALL, "oppositeDirection" : true, "depth" : 25.4 * mm});
        }
    });
